# Revit family: Grinder_Pump-Dual_Seal-Zoeller-7012_7013_Series
name_source: partatom
category: Mechanical Equipment
units: mm (PartAtom-declared; Revit-internal decimal feet)

## family parameters
Always vertical = No
Cut with Voids When Loaded = No
OmniClass Number = 23.60.30.21
OmniClass Title = Pumps
Part Type = Normal
Room Calculation Point = No
Round Connector Dimension = Use Radius
Shared = Yes
Work Plane-Based = Yes

## types (6) — shared parameters
Assembly Code = D2010900
Configuration = High Flow
Cutter & Plate SS Hardened = 55-60 Rockwell
Default Elevation = 0"
Description = Commercial Effluent Pumps
Discharge Diameter = 1.25" NPT
Discharge Radius = 5/8"
Flow @ 5' = 61 GPM
Height = 20 5/8"
Hertz = 60
Impeller Diameter = 6 3/16"
Impeller Trim - Reversing Models Only (Optional) = No
Impeller Type = Bronze Vortex
Installation Type = Floor Mounted
Insulation = Class F
Lead Wires Insulation = Class F
Length = 11 5/8"
Manufacturer = Zoeller
Masterformat Number = 33 36 16
Masterformat Title = Utility Septic Tank Effluent Pumps
Material = Cast Iron-Zoeller-Powder Coated Epoxy
Max. Stator Temp. = 311 °F
Max. Water Temp. = 104 °F
Maximum KW Input = 3.9
Model = 7013
Moisture Sensor (Optional) = Moisture Sensing Probes (Requires a circuit in control panel)
Motor = 2.0 Pump Name Plate Horsepower
Motor Design Letter = NEMA B (3 Ph), NEMA L (1 Ph)
Motor Shaft = 416 S.S.
Motor Thermal Shutoff = Integral On-Lead (1 PH) or Thermal Cut-Out (3 PH)
Motor Type = Submersible
NEC Locked Rotor Code = K
Nominal Height = 5"
O-Rings = Viton
Omniclass Table 23 Code = 23.60.30.21
Omniclass Table 23 Title = Pumps
Operation = Non-Automatic
Overall Height = 23 3/4"
Power Cord = 14 Gauge SOW
Price = Prices may vary. Please consult Manufacturer Representative for most up-to-date price list.
Product Page URL = http://www.zoellerengprod.com
RPM = 3450
Service Factor = 1.2
Shaft Seal Lower (Options) = Silicon Carbide/Silicon Carbide
Shaft Seal Lower Standard = Carbon/Silicon Carbide
Shaft Seal Upper (Options) = Carbon/Silicon Carbide, Silicon Carbide/Silicon Carbide
Shaft Seal Upper Standard = Carbon/Ceramic
Shipping Weight = 137 lbs. (1 PH), 132 lbs. (3 PH)
Tandem Seals = Standard
Type SOW Power Cord Length = 240"
URL = http://www.zoellerengprod.com
Warranty Information = 36 Months (Limited)
Waste Connection = Yes
Width = 8"

## per-type parameters (varying)
| type | Apparent Load | Full Load Amps | Locked Rotor Amps (Voltage Dependant) | Phase | Type | Voltage |
| 7013-200V 1Ph | 4000 VA | 20 A | 60.0 | 1 | Permanent Split Capacitor | 200 V |
| 7013-230V 1Ph | 3956 VA | 17 A | 56.0 | 1 | Permanent Split Capacitor | 230 V |
| 7013-200V 3Ph | 2460 VA | 12 A | 54.0 | 3 | 3 Phase | 200 V |
| 7013-230V 3Ph | 2484 VA | 11 A | 42.0 | 3 | 3 Phase | 230 V |
| 7013-460V 3Ph | 2530 VA | 6 A | 21.0 | 3 | 3 Phase | 460 V |
| 7013-575V 3Ph | 2588 VA | 5 A | 11.0 | 3 | 3 Phase | 575 V |

## geometry (parser evidence)
native form markers: Blend x6, Sweep x3
no freeform markers — native parametric forms only
